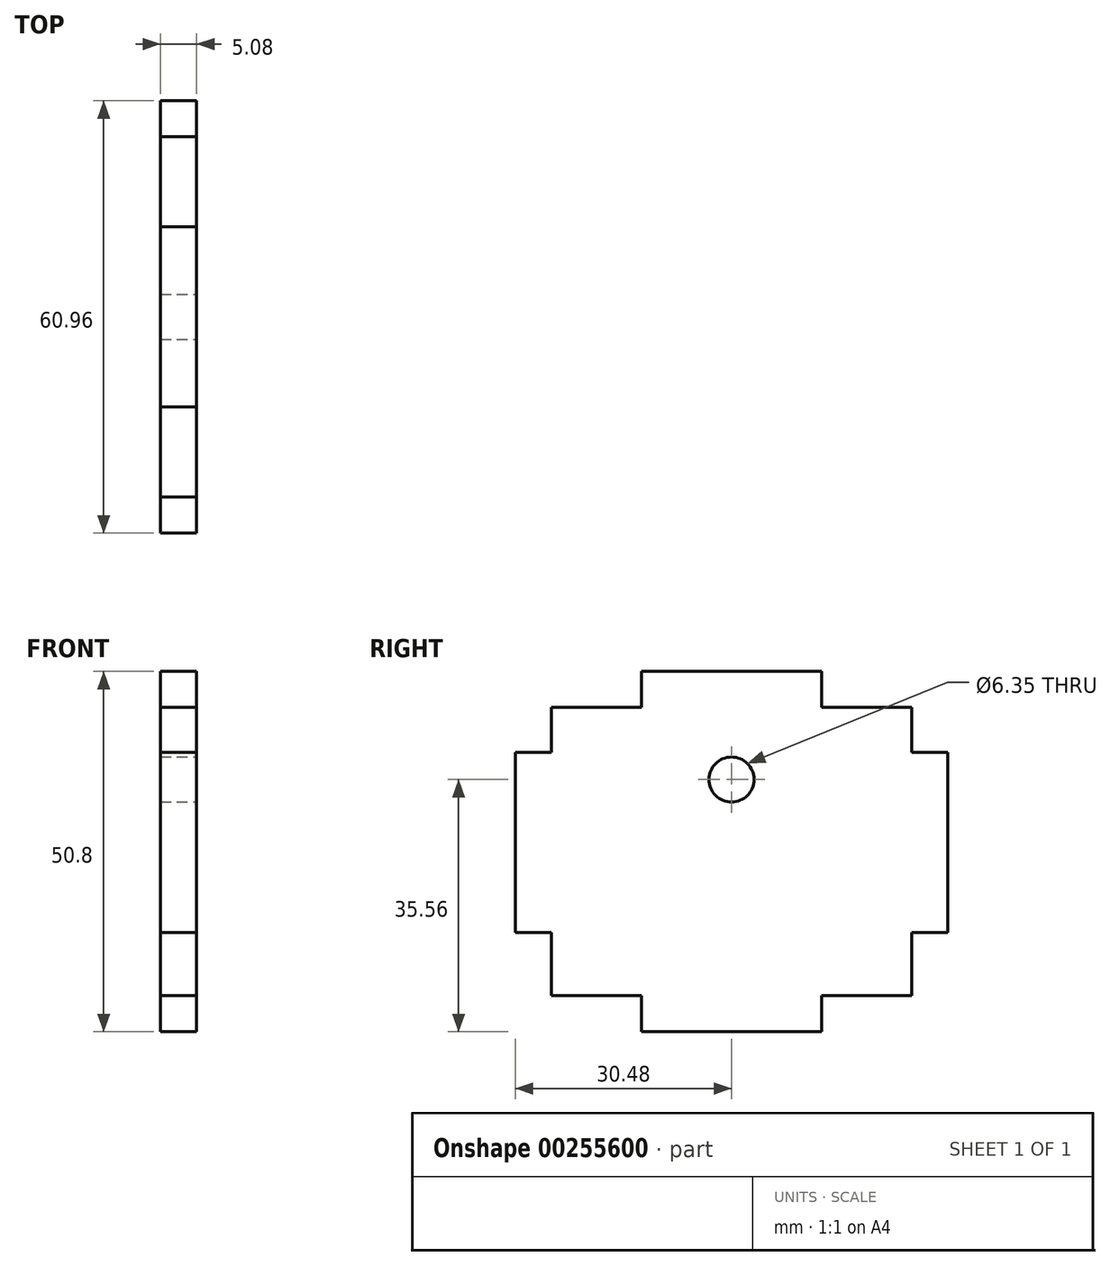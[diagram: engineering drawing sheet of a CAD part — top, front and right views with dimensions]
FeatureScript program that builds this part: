
annotation { "Feature Type Name" : "Feature", "Feature Type Description" : "" }
export const myFeature = defineFeature(function(context is Context, id is Id, definition is map)
    precondition{}
    {
        {
            var Q0;
            Q0=qCreatedBy(makeId("Right.planeOp"),FACE);
            var sketch = newSketch(context, id + "F0", { "sketchPlane" : qUnion([Q0])});
            skLineSegment(sketch, "E0.bottom", {"start": v(12.7, 0) * mm, "end": v(38.1, 0) * mm});
            skLineSegment(sketch, "E0.top", {"start": v(12.7, 50.8) * mm, "end": v(38.1, 50.8) * mm});
            skLineSegment(sketch, "E0.left", {"start": v(0, 5.08) * mm, "end": v(0, 45.72) * mm});
            skLineSegment(sketch, "E0.right", {"start": v(50.8, 5.08) * mm, "end": v(50.8, 45.72) * mm});
            skLineSegment(sketch, "E1.top", {"start": v(0, 45.72) * mm, "end": v(12.7, 45.72) * mm});
            skLineSegment(sketch, "E1.right", {"start": v(12.7, 50.8) * mm, "end": v(12.7, 45.72) * mm});
            skLineSegment(sketch, "E2.top", {"start": v(50.8, 45.72) * mm, "end": v(38.1, 45.72) * mm});
            skLineSegment(sketch, "E2.right", {"start": v(38.1, 50.8) * mm, "end": v(38.1, 45.72) * mm});
            skLineSegment(sketch, "E3.top", {"start": v(0, 5.08) * mm, "end": v(12.7, 5.08) * mm});
            skLineSegment(sketch, "E3.right", {"start": v(12.7, 0) * mm, "end": v(12.7, 5.08) * mm});
            skLineSegment(sketch, "E4.top", {"start": v(50.8, 5.08) * mm, "end": v(38.1, 5.08) * mm});
            skLineSegment(sketch, "E4.right", {"start": v(38.1, 0) * mm, "end": v(38.1, 5.08) * mm});
            skSolve(sketch);
        }
        {
            var Q0;
            Q0=makeQuery(id+"F0.imprint","IMPRINT",FACE,{"disambiguationData":[TD([[makeQuery(id+"F0.imprint","IMPRINT",EDGE,{"derivedFrom":sQuery(id+"F0.wireOp",EDGE,"E0.bottom")}),1.0]])]});
            extrude(context, id + "F1", {"entities" : qUnion([Q0]), "depth" : 5.08 * mm});
        }
        {
            var Q0;
            Q0=makeQuery(id+"F1.opExtrude","CAP_FACE",FACE,{"disambiguationData":[OSD([sQuery(id+"F0.wireOp",EDGE,"E0.bottom"),sQuery(id+"F0.wireOp",EDGE,"E0.top"),sQuery(id+"F0.wireOp",EDGE,"E0.left"),sQuery(id+"F0.wireOp",EDGE,"E0.right"),sQuery(id+"F0.wireOp",EDGE,"E1.top"),sQuery(id+"F0.wireOp",EDGE,"E1.right"),sQuery(id+"F0.wireOp",EDGE,"E2.top"),sQuery(id+"F0.wireOp",EDGE,"E2.right"),sQuery(id+"F0.wireOp",EDGE,"E3.top"),sQuery(id+"F0.wireOp",EDGE,"E3.right"),sQuery(id+"F0.wireOp",EDGE,"E4.top"),sQuery(id+"F0.wireOp",EDGE,"E4.right")])],"isStart":false});
            var sketch = newSketch(context, id + "F2", { "sketchPlane" : qUnion([Q0])});
            skCircle(sketch, "E5", {"center": v(25.4, 35.56) * mm, "radius": 3.18 * mm});
            skSolve(sketch);
        }
        {
            var Q0;
            Q0=makeQuery(id+"F2.imprint","IMPRINT",FACE,{"disambiguationData":[TD([[makeQuery(id+"F2.imprint","IMPRINT",EDGE,{"derivedFrom":sQuery(id+"F2.wireOp",EDGE,"E5")}),1.0]])]});
            var Q1;
            Q1=sQuery(id+"F2.wireOp",EDGE,"E5");
            extrude(context, id + "F3", {"entities" : qUnion([Q0]), "operationType" : NewBodyOperationType.REMOVE, "surfaceEntities" : qUnion([Q1]), "oppositeDirection" : true, "depth" : 25.4 * mm});
        }
        {
            var Q0;
            Q0=makeQuery(id+"F1.opExtrude","CAP_FACE",FACE,{"disambiguationData":[OSD([sQuery(id+"F0.wireOp",EDGE,"E0.bottom"),sQuery(id+"F0.wireOp",EDGE,"E0.top"),sQuery(id+"F0.wireOp",EDGE,"E0.left"),sQuery(id+"F0.wireOp",EDGE,"E0.right"),sQuery(id+"F0.wireOp",EDGE,"E1.top"),sQuery(id+"F0.wireOp",EDGE,"E1.right"),sQuery(id+"F0.wireOp",EDGE,"E2.top"),sQuery(id+"F0.wireOp",EDGE,"E2.right"),sQuery(id+"F0.wireOp",EDGE,"E3.top"),sQuery(id+"F0.wireOp",EDGE,"E3.right"),sQuery(id+"F0.wireOp",EDGE,"E4.top"),sQuery(id+"F0.wireOp",EDGE,"E4.right")])],"isStart":false});
            var sketch = newSketch(context, id + "F4", { "sketchPlane" : qUnion([Q0])});
            skLineSegment(sketch, "E6.bottom", {"start": v(0, 39.37) * mm, "end": v(-5.08, 39.37) * mm});
            skLineSegment(sketch, "E6.top", {"start": v(0, 13.97) * mm, "end": v(-5.08, 13.97) * mm});
            skLineSegment(sketch, "E6.left", {"start": v(0, 39.37) * mm, "end": v(0, 13.97) * mm});
            skLineSegment(sketch, "E6.right", {"start": v(-5.08, 39.37) * mm, "end": v(-5.08, 13.97) * mm});
            skPoint(sketch, "E7.oppositeSnap0", {"position": v(-2.54, 13.97) * mm});
            skLineSegment(sketch, "E7.bottom", {"start": v(50.8, 39.37) * mm, "end": v(55.88, 39.37) * mm});
            skLineSegment(sketch, "E7.top", {"start": v(50.8, 13.97) * mm, "end": v(55.88, 13.97) * mm});
            skLineSegment(sketch, "E7.left", {"start": v(50.8, 39.37) * mm, "end": v(50.8, 13.97) * mm});
            skLineSegment(sketch, "E7.right", {"start": v(55.88, 39.37) * mm, "end": v(55.88, 13.97) * mm});
            skSolve(sketch);
        }
        {
            var Q0;
            Q0 = qSketchRegion(id + "F4", true);
            extrude(context, id + "F5", {"entities" : qUnion([Q0]), "operationType" : NewBodyOperationType.ADD, "oppositeDirection" : true, "depth" : 5.08 * mm});
        }
    });
